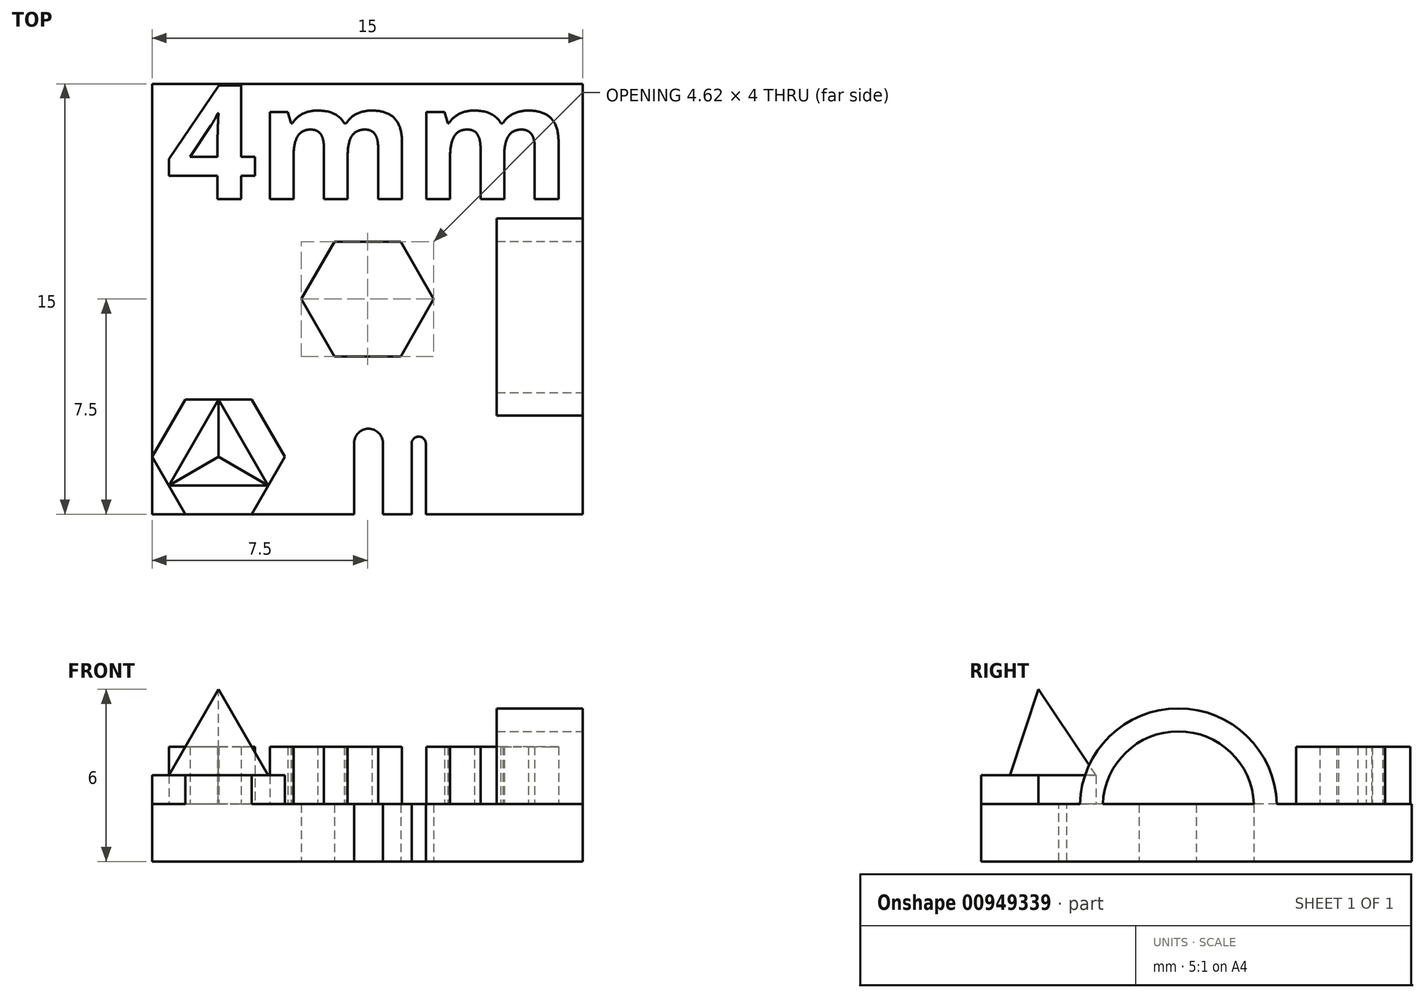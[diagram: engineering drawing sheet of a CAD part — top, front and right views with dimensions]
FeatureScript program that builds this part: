
annotation { "Feature Type Name" : "Feature", "Feature Type Description" : "" }
export const myFeature = defineFeature(function(context is Context, id is Id, definition is map)
    precondition{}
    {
        {
            var Q0;
            Q0=qCreatedBy(makeId("Top.planeOp"),FACE);
            var sketch = newSketch(context, id + "F0", { "sketchPlane" : qUnion([Q0])});
            skLineSegment(sketch, "E0.bottom", {"start": v(-7.5, 7.5) * mm, "end": v(7.5, 7.5) * mm});
            skLineSegment(sketch, "E0.top", {"start": v(-7.5, -7.5) * mm, "end": v(7.5, -7.5) * mm});
            skLineSegment(sketch, "E0.left", {"start": v(-7.5, 7.5) * mm, "end": v(-7.5, -7.5) * mm});
            skLineSegment(sketch, "E0.right", {"start": v(7.5, 7.5) * mm, "end": v(7.5, -7.5) * mm});
            skPoint(sketch, "E0.middle", {"position": v(0, 0) * mm});
            skCircle(sketch, "E1", {"center": v(0, 0) * mm, "radius": 2.3 * mm, "construction": true});
            skLineSegment(sketch, "E2", {"start": v(-1.15, 2) * mm, "end": v(1.15, 2) * mm});
            skLineSegment(sketch, "E3", {"start": v(1.15, 2) * mm, "end": v(2.3, 0) * mm});
            skLineSegment(sketch, "E4", {"start": v(2.3, 0) * mm, "end": v(1.15, -2) * mm});
            skLineSegment(sketch, "E5", {"start": v(1.15, -2) * mm, "end": v(-1.15, -2) * mm});
            skLineSegment(sketch, "E6", {"start": v(-1.15, -2) * mm, "end": v(-2.3, 0) * mm});
            skLineSegment(sketch, "E7", {"start": v(-2.3, 0) * mm, "end": v(-1.15, 2) * mm});
            skSolve(sketch);
        }
        {
            var Q0;
            Q0 = qSketchRegion(id + "F0", true);
            extrude(context, id + "F1", {"entities" : qUnion([Q0]), "depth" : 2 * mm, "offsetDistance" : 25 * mm});
        }
        {
            var Q0;
            Q0=qCreatedBy(makeId("Top.planeOp"),FACE);
            var sketch = newSketch(context, id + "F2", { "sketchPlane" : qUnion([Q0])});
            skText(sketch, "E8", { "text": "4mm", "fontName": "OpenSans-Bold.ttf"});
            const initialGuessF2  = {"E8": [-0.00701, 0.00348, 1, 0, 0.004]};
            skSetInitialGuess(sketch, initialGuessF2);
            skSolve(sketch);
        }
        {
            var Q0;
            Q0 = qSketchRegion(id + "F2", true);
            extrude(context, id + "F3", {"entities" : qUnion([Q0]), "operationType" : NewBodyOperationType.ADD, "depth" : 4 * mm, "offsetDistance" : 25 * mm});
        }
        {
            var Q0;
            Q0=qCreatedBy(makeId("Top.planeOp"),FACE);
            var sketch = newSketch(context, id + "F4", { "sketchPlane" : qUnion([Q0])});
            skCircle(sketch, "E9", {"center": v(-5.2, -5.5) * mm, "radius": 2.3 * mm, "construction": true});
            skLineSegment(sketch, "E10", {"start": v(-6.35, -3.5) * mm, "end": v(-4.04, -3.5) * mm});
            skLineSegment(sketch, "E11", {"start": v(-4.04, -3.5) * mm, "end": v(-2.88, -5.5) * mm});
            skLineSegment(sketch, "E12", {"start": v(-2.88, -5.5) * mm, "end": v(-4.04, -7.5) * mm});
            skLineSegment(sketch, "E13", {"start": v(-4.04, -7.5) * mm, "end": v(-6.35, -7.5) * mm});
            skLineSegment(sketch, "E14", {"start": v(-6.35, -7.5) * mm, "end": v(-7.5, -5.5) * mm});
            skLineSegment(sketch, "E15", {"start": v(-7.5, -5.5) * mm, "end": v(-6.35, -3.5) * mm});
            skSolve(sketch);
        }
        {
            var Q0;
            Q0 = qSketchRegion(id + "F4", true);
            extrude(context, id + "F5", {"entities" : qUnion([Q0]), "operationType" : NewBodyOperationType.ADD, "depth" : 3 * mm, "offsetDistance" : 25 * mm});
        }
        {
            var Q0;
            Q0=makeQuery(id+"F1.opExtrude","SWEPT_FACE",FACE,{"disambiguationData":[OSD([sQuery(id+"F0.wireOp",EDGE,"E0.right")])]});
            var sketch = newSketch(context, id + "F6", { "sketchPlane" : qUnion([Q0])});
            skArc(sketch, "E16", {"start": v(2, 2) * mm, "mid": v(-0.63, 4.53) * mm, "end": v(-3.26, 2) * mm});
            skArc(sketch, "E17.0", {"start": v(2.8, 2) * mm, "mid": v(-0.63, 5.33) * mm, "end": v(-4.06, 2) * mm});
            skLineSegment(sketch, "E18", {"start": v(-4.06, 2) * mm, "end": v(-3.26, 2) * mm});
            skLineSegment(sketch, "E19", {"start": v(2, 2) * mm, "end": v(2.8, 2) * mm});
            skSolve(sketch);
        }
        {
            var Q0;
            Q0 = qSketchRegion(id + "F6", true);
            extrude(context, id + "F7", {"entities" : qUnion([Q0]), "operationType" : NewBodyOperationType.ADD, "depth" : -3 * mm, "offsetDistance" : 25 * mm});
        }
        {
            var Q0;
            Q0=makeQuery(id+"F5.opExtrude","CAP_FACE",FACE,{"disambiguationData":[OSD([sQuery(id+"F4.wireOp",EDGE,"E10"),sQuery(id+"F4.wireOp",EDGE,"E11"),sQuery(id+"F4.wireOp",EDGE,"E12"),sQuery(id+"F4.wireOp",EDGE,"E13"),sQuery(id+"F4.wireOp",EDGE,"E14"),sQuery(id+"F4.wireOp",EDGE,"E15")])],"isStart":false});
            cPlane(context, id + "F8", {"entities" : qUnion([Q0]), "cplaneType" : CPlaneType.OFFSET, "offset" : 3 * mm, "width" : 150 * mm, "height" : 150 * mm});
        }
        {
            var Q0;
            Q0=makeQuery(id+"F5.opExtrude","CAP_FACE",FACE,{"disambiguationData":[OSD([sQuery(id+"F4.wireOp",EDGE,"E10"),sQuery(id+"F4.wireOp",EDGE,"E11"),sQuery(id+"F4.wireOp",EDGE,"E12"),sQuery(id+"F4.wireOp",EDGE,"E13"),sQuery(id+"F4.wireOp",EDGE,"E14"),sQuery(id+"F4.wireOp",EDGE,"E15")])],"isStart":false});
            var sketch = newSketch(context, id + "F9", { "sketchPlane" : qUnion([Q0])});
            skCircle(sketch, "E20.cCircle", {"center": v(-5.2, -5.5) * mm, "radius": 1 * mm, "construction": true});
            skLineSegment(sketch, "E20.0", {"start": v(-3.46, -6.5) * mm, "end": v(-6.92, -6.5) * mm});
            skLineSegment(sketch, "E20.1", {"start": v(-6.92, -6.5) * mm, "end": v(-5.2, -3.5) * mm});
            skLineSegment(sketch, "E20.2", {"start": v(-5.2, -3.5) * mm, "end": v(-3.46, -6.5) * mm});
            skPoint(sketch, "E20.0.midPoint", {"position": v(-5.2, -6.5) * mm});
            skSolve(sketch);
        }
        {
            var Q0;
            Q0=qCreatedBy(id+"F8.planeOp",FACE);
            var sketch = newSketch(context, id + "F10", { "sketchPlane" : qUnion([Q0])});
            skPoint(sketch, "E21", {"position": v(-5.19, -5.5) * mm});
            skSolve(sketch);
        }
        {
            var Q0;
            Q0=makeQuery(id+"F9.imprint","IMPRINT",FACE,{"disambiguationData":[TD([[makeQuery(id+"F9.imprint","IMPRINT",EDGE,{"derivedFrom":sQuery(id+"F9.wireOp",EDGE,"E20.0")}),-1.0]])]});
            var Q1;
            Q1=sQuery(id+"F10.wireOp",VERTEX,"E21");
            loft(context, id + "F11", {"sheetProfilesArray" : [{ "sheetProfileEntities" : qUnion([Q0]) }, { "sheetProfileEntities" : qUnion([Q1]) }]});
        }
        {
            var Q0;
            {var subQ0=makeQuery(id+"F3.opExtrude","SWEPT_FACE",FACE,{"disambiguationData":[OSD([sQuery(id+"F2.wireOp",EDGE,"E8.sketch_text.stroke-88")])]});var subQ1=makeQuery(id+"F3.opExtrude","SWEPT_FACE",FACE,{"disambiguationData":[OSD([sQuery(id+"F2.wireOp",EDGE,"E8.sketch_text.stroke-86")])]});var subQ2=makeQuery(id+"F3.opExtrude","SWEPT_FACE",FACE,{"disambiguationData":[OSD([sQuery(id+"F2.wireOp",EDGE,"E8.sketch_text.stroke-85")])]});var subQ3=makeQuery(id+"F3.opExtrude","SWEPT_FACE",FACE,{"disambiguationData":[OSD([sQuery(id+"F2.wireOp",EDGE,"E8.sketch_text.stroke-84")])]});var subQ4=makeQuery(id+"F3.opExtrude","SWEPT_FACE",FACE,{"disambiguationData":[OSD([sQuery(id+"F2.wireOp",EDGE,"E8.sketch_text.stroke-83")])]});var subQ5=makeQuery(id+"F3.opExtrude","SWEPT_FACE",FACE,{"disambiguationData":[OSD([sQuery(id+"F2.wireOp",EDGE,"E8.sketch_text.stroke-82")])]});var subQ6=makeQuery(id+"F3.opExtrude","SWEPT_FACE",FACE,{"disambiguationData":[OSD([sQuery(id+"F2.wireOp",EDGE,"E8.sketch_text.stroke-81")])]});var subQ7=makeQuery(id+"F3.opExtrude","SWEPT_FACE",FACE,{"disambiguationData":[OSD([sQuery(id+"F2.wireOp",EDGE,"E8.sketch_text.stroke-70")])]});var subQ8=makeQuery(id+"F3.opExtrude","SWEPT_FACE",FACE,{"disambiguationData":[OSD([sQuery(id+"F2.wireOp",EDGE,"E8.sketch_text.stroke-68")])]});var subQ9=makeQuery(id+"F3.opExtrude","SWEPT_FACE",FACE,{"disambiguationData":[OSD([sQuery(id+"F2.wireOp",EDGE,"E8.sketch_text.stroke-67")])]});var subQ10=makeQuery(id+"F3.opExtrude","SWEPT_FACE",FACE,{"disambiguationData":[OSD([sQuery(id+"F2.wireOp",EDGE,"E8.sketch_text.stroke-66")])]});var subQ11=makeQuery(id+"F3.opExtrude","SWEPT_FACE",FACE,{"disambiguationData":[OSD([sQuery(id+"F2.wireOp",EDGE,"E8.sketch_text.stroke-65")])]});var subQ12=makeQuery(id+"F3.opExtrude","SWEPT_FACE",FACE,{"disambiguationData":[OSD([sQuery(id+"F2.wireOp",EDGE,"E8.sketch_text.stroke-64")])]});var subQ13=makeQuery(id+"F3.opExtrude","SWEPT_FACE",FACE,{"disambiguationData":[OSD([sQuery(id+"F2.wireOp",EDGE,"E8.sketch_text.stroke-63")])]});var subQ14=makeQuery(id+"F3.opExtrude","SWEPT_FACE",FACE,{"disambiguationData":[OSD([sQuery(id+"F2.wireOp",EDGE,"E8.sketch_text.stroke-62")])]});var subQ15=makeQuery(id+"F3.opExtrude","SWEPT_FACE",FACE,{"disambiguationData":[OSD([sQuery(id+"F2.wireOp",EDGE,"E8.sketch_text.stroke-61")])]});var subQ16=makeQuery(id+"F3.opExtrude","SWEPT_FACE",FACE,{"disambiguationData":[OSD([sQuery(id+"F2.wireOp",EDGE,"E8.sketch_text.stroke-60")])]});var subQ17=makeQuery(id+"F3.opExtrude","SWEPT_FACE",FACE,{"disambiguationData":[OSD([sQuery(id+"F2.wireOp",EDGE,"E8.sketch_text.stroke-53")])]});var subQ18=makeQuery(id+"F3.opExtrude","SWEPT_FACE",FACE,{"disambiguationData":[OSD([sQuery(id+"F2.wireOp",EDGE,"E8.sketch_text.stroke-52")])]});var subQ19=makeQuery(id+"F3.opExtrude","SWEPT_FACE",FACE,{"disambiguationData":[OSD([sQuery(id+"F2.wireOp",EDGE,"E8.sketch_text.stroke-51")])]});var subQ20=makeQuery(id+"F3.opExtrude","SWEPT_FACE",FACE,{"disambiguationData":[OSD([sQuery(id+"F2.wireOp",EDGE,"E8.sketch_text.stroke-50")])]});var subQ21=makeQuery(id+"F3.opExtrude","SWEPT_FACE",FACE,{"disambiguationData":[OSD([sQuery(id+"F2.wireOp",EDGE,"E8.sketch_text.stroke-49")])]});var subQ22=makeQuery(id+"F3.opExtrude","SWEPT_FACE",FACE,{"disambiguationData":[OSD([sQuery(id+"F2.wireOp",EDGE,"E8.sketch_text.stroke-48")])]});var subQ23=makeQuery(id+"F3.opExtrude","SWEPT_FACE",FACE,{"disambiguationData":[OSD([sQuery(id+"F2.wireOp",EDGE,"E8.sketch_text.stroke-47")])]});var subQ24=makeQuery(id+"F3.opExtrude","SWEPT_FACE",FACE,{"disambiguationData":[OSD([sQuery(id+"F2.wireOp",EDGE,"E8.sketch_text.stroke-46")])]});var subQ25=makeQuery(id+"F3.opExtrude","SWEPT_FACE",FACE,{"disambiguationData":[OSD([sQuery(id+"F2.wireOp",EDGE,"E8.sketch_text.stroke-45")])]});var subQ26=makeQuery(id+"F3.opExtrude","SWEPT_FACE",FACE,{"disambiguationData":[OSD([sQuery(id+"F2.wireOp",EDGE,"E8.sketch_text.stroke-44")])]});var subQ27=makeQuery(id+"F3.opExtrude","SWEPT_FACE",FACE,{"disambiguationData":[OSD([sQuery(id+"F2.wireOp",EDGE,"E8.sketch_text.stroke-43")])]});var subQ28=makeQuery(id+"F3.opExtrude","SWEPT_FACE",FACE,{"disambiguationData":[OSD([sQuery(id+"F2.wireOp",EDGE,"E8.sketch_text.stroke-42")])]});var subQ29=makeQuery(id+"F3.opExtrude","SWEPT_FACE",FACE,{"disambiguationData":[OSD([sQuery(id+"F2.wireOp",EDGE,"E8.sketch_text.stroke-41")])]});var subQ30=makeQuery(id+"F3.opExtrude","SWEPT_FACE",FACE,{"disambiguationData":[OSD([sQuery(id+"F2.wireOp",EDGE,"E8.sketch_text.stroke-40")])]});var subQ31=makeQuery(id+"F3.opExtrude","SWEPT_FACE",FACE,{"disambiguationData":[OSD([sQuery(id+"F2.wireOp",EDGE,"E8.sketch_text.stroke-10")])]});var subQ32=makeQuery(id+"F3.opExtrude","SWEPT_FACE",FACE,{"disambiguationData":[OSD([sQuery(id+"F2.wireOp",EDGE,"E8.sketch_text.stroke-9")])]});var subQ33=makeQuery(id+"F3.opExtrude","SWEPT_FACE",FACE,{"disambiguationData":[OSD([sQuery(id+"F2.wireOp",EDGE,"E8.sketch_text.stroke-95")])]});var subQ34=makeQuery(id+"F3.opExtrude","SWEPT_FACE",FACE,{"disambiguationData":[OSD([sQuery(id+"F2.wireOp",EDGE,"E8.sketch_text.stroke-8")])]});var subQ35=makeQuery(id+"F3.opExtrude","SWEPT_FACE",FACE,{"disambiguationData":[OSD([sQuery(id+"F2.wireOp",EDGE,"E8.sketch_text.stroke-94")])]});var subQ36=makeQuery(id+"F3.opExtrude","SWEPT_FACE",FACE,{"disambiguationData":[OSD([sQuery(id+"F2.wireOp",EDGE,"E8.sketch_text.stroke-7")])]});var subQ37=makeQuery(id+"F3.opExtrude","SWEPT_FACE",FACE,{"disambiguationData":[OSD([sQuery(id+"F2.wireOp",EDGE,"E8.sketch_text.stroke-93")])]});var subQ38=makeQuery(id+"F3.opExtrude","SWEPT_FACE",FACE,{"disambiguationData":[OSD([sQuery(id+"F2.wireOp",EDGE,"E8.sketch_text.stroke-6")])]});var subQ39=makeQuery(id+"F3.opExtrude","SWEPT_FACE",FACE,{"disambiguationData":[OSD([sQuery(id+"F2.wireOp",EDGE,"E8.sketch_text.stroke-92")])]});var subQ40=makeQuery(id+"F3.opExtrude","SWEPT_FACE",FACE,{"disambiguationData":[OSD([sQuery(id+"F2.wireOp",EDGE,"E8.sketch_text.stroke-5")])]});var subQ41=makeQuery(id+"F3.opExtrude","SWEPT_FACE",FACE,{"disambiguationData":[OSD([sQuery(id+"F2.wireOp",EDGE,"E8.sketch_text.stroke-80")])]});var subQ42=sQuery(id+"F0.wireOp",EDGE,"E7");var subQ43=makeQuery(id+"F1.opExtrude","SWEPT_FACE",FACE,{"disambiguationData":[OSD([subQ42])]});var subQ44=makeQuery(id+"F3.opExtrude","SWEPT_FACE",FACE,{"disambiguationData":[OSD([sQuery(id+"F2.wireOp",EDGE,"E8.sketch_text.stroke-87")])]});var subQ45=makeQuery(id+"F3.opExtrude","SWEPT_FACE",FACE,{"disambiguationData":[OSD([sQuery(id+"F2.wireOp",EDGE,"E8.sketch_text.stroke-0")])]});var subQ46=makeQuery(id+"F3.opExtrude","SWEPT_FACE",FACE,{"disambiguationData":[OSD([sQuery(id+"F2.wireOp",EDGE,"E8.sketch_text.stroke-73")])]});var subQ47=sQuery(id+"F0.wireOp",EDGE,"E0.left");var subQ48=makeQuery(id+"F1.opExtrude","SWEPT_FACE",FACE,{"disambiguationData":[OSD([subQ47])]});var subQ49=makeQuery(id+"F3.opExtrude","SWEPT_FACE",FACE,{"disambiguationData":[OSD([sQuery(id+"F2.wireOp",EDGE,"E8.sketch_text.stroke-19")])]});var subQ50=makeQuery(id+"F3.opExtrude","SWEPT_FACE",FACE,{"disambiguationData":[OSD([sQuery(id+"F2.wireOp",EDGE,"E8.sketch_text.stroke-72")])]});var subQ51=sQuery(id+"F0.wireOp",EDGE,"E0.top");var subQ52=makeQuery(id+"F1.opExtrude","SWEPT_FACE",FACE,{"disambiguationData":[OSD([subQ51])]});var subQ53=makeQuery(id+"F3.opExtrude","SWEPT_FACE",FACE,{"disambiguationData":[OSD([sQuery(id+"F2.wireOp",EDGE,"E8.sketch_text.stroke-18")])]});var subQ54=makeQuery(id+"F3.opExtrude","SWEPT_FACE",FACE,{"disambiguationData":[OSD([sQuery(id+"F2.wireOp",EDGE,"E8.sketch_text.stroke-71")])]});var subQ55=sQuery(id+"F0.wireOp",EDGE,"E6");var subQ56=sQuery(id+"F0.wireOp",EDGE,"E5");var subQ57=sQuery(id+"F0.wireOp",EDGE,"E4");var subQ58=sQuery(id+"F0.wireOp",EDGE,"E3");var subQ59=sQuery(id+"F0.wireOp",EDGE,"E2");var subQ60=sQuery(id+"F0.wireOp",EDGE,"E0.right");var subQ61=sQuery(id+"F0.wireOp",EDGE,"E0.bottom");var subQ62=makeQuery(id+"F1.opExtrude","CAP_FACE",FACE,{"disambiguationData":[OSD([subQ61,subQ51,subQ47,subQ60,subQ59,subQ58,subQ57,subQ56,subQ55,subQ42])],"isStart":false});var subQ63=makeQuery(id+"F3.opExtrude","SWEPT_FACE",FACE,{"disambiguationData":[OSD([sQuery(id+"F2.wireOp",EDGE,"E8.sketch_text.stroke-17")])]});var subQ64=makeQuery(id+"F3.opExtrude","SWEPT_FACE",FACE,{"disambiguationData":[OSD([sQuery(id+"F2.wireOp",EDGE,"E8.sketch_text.stroke-69")])]});var subQ65=makeQuery(id+"F1.opExtrude","SWEPT_FACE",FACE,{"disambiguationData":[OSD([subQ61])]});var subQ66=makeQuery(id+"F3.opExtrude","SWEPT_FACE",FACE,{"disambiguationData":[OSD([sQuery(id+"F2.wireOp",EDGE,"E8.sketch_text.stroke-15")])]});var subQ67=makeQuery(id+"F3.opExtrude","SWEPT_FACE",FACE,{"disambiguationData":[OSD([sQuery(id+"F2.wireOp",EDGE,"E8.sketch_text.stroke-74")])]});var subQ68=makeQuery(id+"F1.opExtrude","SWEPT_FACE",FACE,{"disambiguationData":[OSD([subQ60])]});var subQ69=makeQuery(id+"F3.opExtrude","SWEPT_FACE",FACE,{"disambiguationData":[OSD([sQuery(id+"F2.wireOp",EDGE,"E8.sketch_text.stroke-20")])]});var subQ70=makeQuery(id+"F3.opExtrude","SWEPT_FACE",FACE,{"disambiguationData":[OSD([sQuery(id+"F2.wireOp",EDGE,"E8.sketch_text.stroke-75")])]});var subQ71=makeQuery(id+"F1.opExtrude","SWEPT_FACE",FACE,{"disambiguationData":[OSD([subQ59])]});var subQ72=makeQuery(id+"F3.opExtrude","SWEPT_FACE",FACE,{"disambiguationData":[OSD([sQuery(id+"F2.wireOp",EDGE,"E8.sketch_text.stroke-21")])]});var subQ73=makeQuery(id+"F3.opExtrude","SWEPT_FACE",FACE,{"disambiguationData":[OSD([sQuery(id+"F2.wireOp",EDGE,"E8.sketch_text.stroke-1")])]});var subQ74=makeQuery(id+"F3.opExtrude","SWEPT_FACE",FACE,{"disambiguationData":[OSD([sQuery(id+"F2.wireOp",EDGE,"E8.sketch_text.stroke-76")])]});var subQ75=makeQuery(id+"F1.opExtrude","SWEPT_FACE",FACE,{"disambiguationData":[OSD([subQ58])]});var subQ76=makeQuery(id+"F3.opExtrude","SWEPT_FACE",FACE,{"disambiguationData":[OSD([sQuery(id+"F2.wireOp",EDGE,"E8.sketch_text.stroke-22")])]});var subQ77=makeQuery(id+"F3.opExtrude","SWEPT_FACE",FACE,{"disambiguationData":[OSD([sQuery(id+"F2.wireOp",EDGE,"E8.sketch_text.stroke-89")])]});var subQ78=makeQuery(id+"F3.opExtrude","SWEPT_FACE",FACE,{"disambiguationData":[OSD([sQuery(id+"F2.wireOp",EDGE,"E8.sketch_text.stroke-2")])]});var subQ79=makeQuery(id+"F3.opExtrude","SWEPT_FACE",FACE,{"disambiguationData":[OSD([sQuery(id+"F2.wireOp",EDGE,"E8.sketch_text.stroke-77")])]});var subQ80=makeQuery(id+"F1.opExtrude","SWEPT_FACE",FACE,{"disambiguationData":[OSD([subQ57])]});var subQ81=makeQuery(id+"F3.opExtrude","SWEPT_FACE",FACE,{"disambiguationData":[OSD([sQuery(id+"F2.wireOp",EDGE,"E8.sketch_text.stroke-23")])]});var subQ82=makeQuery(id+"F3.opExtrude","SWEPT_FACE",FACE,{"disambiguationData":[OSD([sQuery(id+"F2.wireOp",EDGE,"E8.sketch_text.stroke-90")])]});var subQ83=makeQuery(id+"F3.opExtrude","SWEPT_FACE",FACE,{"disambiguationData":[OSD([sQuery(id+"F2.wireOp",EDGE,"E8.sketch_text.stroke-3")])]});var subQ84=makeQuery(id+"F3.opExtrude","SWEPT_FACE",FACE,{"disambiguationData":[OSD([sQuery(id+"F2.wireOp",EDGE,"E8.sketch_text.stroke-78")])]});var subQ85=makeQuery(id+"F1.opExtrude","SWEPT_FACE",FACE,{"disambiguationData":[OSD([subQ56])]});var subQ86=makeQuery(id+"F3.opExtrude","SWEPT_FACE",FACE,{"disambiguationData":[OSD([sQuery(id+"F2.wireOp",EDGE,"E8.sketch_text.stroke-24")])]});var subQ87=makeQuery(id+"F3.opExtrude","SWEPT_FACE",FACE,{"disambiguationData":[OSD([sQuery(id+"F2.wireOp",EDGE,"E8.sketch_text.stroke-91")])]});var subQ88=makeQuery(id+"F3.opExtrude","SWEPT_FACE",FACE,{"disambiguationData":[OSD([sQuery(id+"F2.wireOp",EDGE,"E8.sketch_text.stroke-4")])]});var subQ89=makeQuery(id+"F3.opExtrude","SWEPT_FACE",FACE,{"disambiguationData":[OSD([sQuery(id+"F2.wireOp",EDGE,"E8.sketch_text.stroke-79")])]});var subQ90=makeQuery(id+"F1.opExtrude","SWEPT_FACE",FACE,{"disambiguationData":[OSD([subQ55])]});var subQ91=makeQuery(id+"F3.opExtrude","SWEPT_FACE",FACE,{"disambiguationData":[OSD([sQuery(id+"F2.wireOp",EDGE,"E8.sketch_text.stroke-25")])]});var subQ92=makeQuery(id+"F3.opExtrude","SWEPT_FACE",FACE,{"disambiguationData":[OSD([sQuery(id+"F2.wireOp",EDGE,"E8.sketch_text.stroke-11")])]});var subQ93=makeQuery(id+"F3.opExtrude","SWEPT_FACE",FACE,{"disambiguationData":[OSD([sQuery(id+"F2.wireOp",EDGE,"E8.sketch_text.stroke-12")])]});var subQ94=makeQuery(id+"F3.opExtrude","SWEPT_FACE",FACE,{"disambiguationData":[OSD([sQuery(id+"F2.wireOp",EDGE,"E8.sketch_text.stroke-13")])]});var subQ95=makeQuery(id+"F3.opExtrude","SWEPT_FACE",FACE,{"disambiguationData":[OSD([sQuery(id+"F2.wireOp",EDGE,"E8.sketch_text.stroke-14")])]});var subQ96=makeQuery(id+"F3.opExtrude","SWEPT_FACE",FACE,{"disambiguationData":[OSD([sQuery(id+"F2.wireOp",EDGE,"E8.sketch_text.stroke-16")])]});var subQ97=makeQuery(id+"F3.opExtrude","SWEPT_FACE",FACE,{"disambiguationData":[OSD([sQuery(id+"F2.wireOp",EDGE,"E8.sketch_text.stroke-31")])]});var subQ98=makeQuery(id+"F3.opExtrude","SWEPT_FACE",FACE,{"disambiguationData":[OSD([sQuery(id+"F2.wireOp",EDGE,"E8.sketch_text.stroke-32")])]});var subQ99=makeQuery(id+"F3.opExtrude","SWEPT_FACE",FACE,{"disambiguationData":[OSD([sQuery(id+"F2.wireOp",EDGE,"E8.sketch_text.stroke-33")])]});var subQ100=makeQuery(id+"F3.opExtrude","SWEPT_FACE",FACE,{"disambiguationData":[OSD([sQuery(id+"F2.wireOp",EDGE,"E8.sketch_text.stroke-34")])]});var subQ101=makeQuery(id+"F3.opExtrude","SWEPT_FACE",FACE,{"disambiguationData":[OSD([sQuery(id+"F2.wireOp",EDGE,"E8.sketch_text.stroke-35")])]});var subQ102=makeQuery(id+"F3.opExtrude","SWEPT_FACE",FACE,{"disambiguationData":[OSD([sQuery(id+"F2.wireOp",EDGE,"E8.sketch_text.stroke-36")])]});var subQ103=makeQuery(id+"F3.opExtrude","SWEPT_FACE",FACE,{"disambiguationData":[OSD([sQuery(id+"F2.wireOp",EDGE,"E8.sketch_text.stroke-37")])]});var subQ104=makeQuery(id+"F3.opExtrude","SWEPT_FACE",FACE,{"disambiguationData":[OSD([sQuery(id+"F2.wireOp",EDGE,"E8.sketch_text.stroke-38")])]});var subQ105=makeQuery(id+"F3.opExtrude","SWEPT_FACE",FACE,{"disambiguationData":[OSD([sQuery(id+"F2.wireOp",EDGE,"E8.sketch_text.stroke-39")])]});var subQ106=makeQuery(id+"F3.opExtrude","SWEPT_FACE",FACE,{"disambiguationData":[OSD([sQuery(id+"F2.wireOp",EDGE,"E8.sketch_text.stroke-96")])]});var subQ107=makeQuery(id+"F3.opExtrude","SWEPT_FACE",FACE,{"disambiguationData":[OSD([sQuery(id+"F2.wireOp",EDGE,"E8.sketch_text.stroke-97")])]});var subQ108=makeQuery(id+"F3.opExtrude","SWEPT_FACE",FACE,{"disambiguationData":[OSD([sQuery(id+"F2.wireOp",EDGE,"E8.sketch_text.stroke-98")])]});var subQ109=makeQuery(id+"F3.opExtrude","SWEPT_FACE",FACE,{"disambiguationData":[OSD([sQuery(id+"F2.wireOp",EDGE,"E8.sketch_text.stroke-99")])]});var subQ110=makeQuery(id+"F3.opExtrude","SWEPT_FACE",FACE,{"disambiguationData":[OSD([sQuery(id+"F2.wireOp",EDGE,"E8.sketch_text.stroke-100")])]});var subQ111=makeQuery(id+"F3.opExtrude","SWEPT_FACE",FACE,{"disambiguationData":[OSD([sQuery(id+"F2.wireOp",EDGE,"E8.sketch_text.stroke-101")])]});var subQ112=makeQuery(id+"F3.opExtrude","SWEPT_FACE",FACE,{"disambiguationData":[OSD([sQuery(id+"F2.wireOp",EDGE,"E8.sketch_text.stroke-102")])]});var subQ113=makeQuery(id+"F3.opExtrude","SWEPT_FACE",FACE,{"disambiguationData":[OSD([sQuery(id+"F2.wireOp",EDGE,"E8.sketch_text.stroke-103")])]});var subQ114=makeQuery(id+"F3.opExtrude","SWEPT_FACE",FACE,{"disambiguationData":[OSD([sQuery(id+"F2.wireOp",EDGE,"E8.sketch_text.stroke-104")])]});var subQ115=makeQuery(id+"F3.opExtrude","SWEPT_FACE",FACE,{"disambiguationData":[OSD([sQuery(id+"F2.wireOp",EDGE,"E8.sketch_text.stroke-105")])]});var subQ116=makeQuery(id+"F3.opExtrude","SWEPT_FACE",FACE,{"disambiguationData":[OSD([sQuery(id+"F2.wireOp",EDGE,"E8.sketch_text.stroke-106")])]});var subQ117=makeQuery(id+"F3.opExtrude","SWEPT_FACE",FACE,{"disambiguationData":[OSD([sQuery(id+"F2.wireOp",EDGE,"E8.sketch_text.stroke-107")])]});var subQ118=makeQuery(id+"F3.opExtrude","SWEPT_FACE",FACE,{"disambiguationData":[OSD([sQuery(id+"F2.wireOp",EDGE,"E8.sketch_text.stroke-108")])]});var subQ119=makeQuery(id+"F3.opExtrude","SWEPT_FACE",FACE,{"disambiguationData":[OSD([sQuery(id+"F2.wireOp",EDGE,"E8.sketch_text.stroke-109")])]});var subQ120=makeQuery(id+"F3.opExtrude","SWEPT_FACE",FACE,{"disambiguationData":[OSD([sQuery(id+"F2.wireOp",EDGE,"E8.sketch_text.stroke-110")])]});var subQ121=makeQuery(id+"F3.opExtrude","SWEPT_FACE",FACE,{"disambiguationData":[OSD([sQuery(id+"F2.wireOp",EDGE,"E8.sketch_text.stroke-111")])]});var subQ122=makeQuery(id+"F3.opExtrude","SWEPT_FACE",FACE,{"disambiguationData":[OSD([sQuery(id+"F2.wireOp",EDGE,"E8.sketch_text.stroke-112")])]});var subQ123=makeQuery(id+"F3.opExtrude","SWEPT_FACE",FACE,{"disambiguationData":[OSD([sQuery(id+"F2.wireOp",EDGE,"E8.sketch_text.stroke-113")])]});var subQ124=makeQuery(id+"F3.opExtrude","SWEPT_FACE",FACE,{"disambiguationData":[OSD([sQuery(id+"F2.wireOp",EDGE,"E8.sketch_text.stroke-114")])]});var subQ125=makeQuery(id+"F3.opExtrude","SWEPT_FACE",FACE,{"disambiguationData":[OSD([sQuery(id+"F2.wireOp",EDGE,"E8.sketch_text.stroke-115")])]});Q0=makeQuery(id+"F5.boolean.opBoolean","SPLIT",FACE,{"disambiguationData":[TD([subQ65,subQ62,subQ52,subQ48,subQ68,subQ71,subQ75,subQ80,subQ85,subQ90,subQ43,subQ45,subQ73,subQ78,subQ83,subQ88,subQ40,subQ38,subQ36,subQ34,subQ32,subQ31,subQ92,subQ93,subQ94,subQ95,subQ66,subQ96,subQ63,subQ53,subQ49,subQ69,subQ72,subQ76,subQ81,subQ86,subQ91,subQ97,subQ98,subQ99,subQ100,subQ101,subQ102,subQ103,subQ104,subQ105,subQ30,subQ29,subQ28,subQ27,subQ26,subQ25,subQ24,subQ23,subQ22,subQ21,subQ20,subQ19,subQ18,subQ17,subQ16,subQ15,subQ14,subQ13,subQ12,subQ11,subQ10,subQ9,subQ8,subQ64,subQ7,subQ54,subQ50,subQ46,subQ67,subQ70,subQ74,subQ79,subQ84,subQ89,subQ41,subQ6,subQ5,subQ4,subQ3,subQ2,subQ1,subQ44,subQ0,subQ77,subQ82,subQ87,subQ39,subQ37,subQ35,subQ33,subQ106,subQ107,subQ108,subQ109,subQ110,subQ111,subQ112,subQ113,subQ114,subQ115,subQ116,subQ117,subQ118,subQ119,subQ120,subQ121,subQ122,subQ123,subQ124,subQ125,makeQuery(id+"F5.opExtrude","SWEPT_FACE",FACE,{"disambiguationData":[OSD([sQuery(id+"F4.wireOp",EDGE,"E10")])]}),makeQuery(id+"F5.opExtrude","SWEPT_FACE",FACE,{"disambiguationData":[OSD([sQuery(id+"F4.wireOp",EDGE,"E11")])]}),makeQuery(id+"F5.opExtrude","SWEPT_FACE",FACE,{"disambiguationData":[OSD([sQuery(id+"F4.wireOp",EDGE,"E12")])]}),makeQuery(id+"F5.opExtrude","SWEPT_FACE",FACE,{"disambiguationData":[OSD([sQuery(id+"F4.wireOp",EDGE,"E13")])]}),makeQuery(id+"F5.opExtrude","SWEPT_FACE",FACE,{"disambiguationData":[OSD([sQuery(id+"F4.wireOp",EDGE,"E14")])]}),makeQuery(id+"F5.opExtrude","SWEPT_FACE",FACE,{"disambiguationData":[OSD([sQuery(id+"F4.wireOp",EDGE,"E15")])]})])],"derivedFrom":makeQuery(id+"F3.boolean.opBoolean","SPLIT",FACE,{"disambiguationData":[TD([subQ65])],"derivedFrom":subQ62})});}
            var sketch = newSketch(context, id + "F12", { "sketchPlane" : qUnion([Q0])});
            skLineSegment(sketch, "E22", {"start": v(-0.46, -7.5) * mm, "end": v(-0.46, -5.02) * mm});
            skLineSegment(sketch, "E23", {"start": v(0.54, -5.02) * mm, "end": v(0.54, -7.5) * mm});
            skLineSegment(sketch, "E24", {"start": v(1.54, -7.5) * mm, "end": v(1.54, -5.05) * mm});
            skLineSegment(sketch, "E25", {"start": v(2.04, -5.05) * mm, "end": v(2.04, -7.5) * mm});
            skLineSegment(sketch, "E26", {"start": v(-0.46, -7.5) * mm, "end": v(0.54, -7.5) * mm});
            skLineSegment(sketch, "E27", {"start": v(1.54, -7.5) * mm, "end": v(2.04, -7.5) * mm});
            skArc(sketch, "E28", {"start": v(0.54, -5.02) * mm, "mid": v(0.04, -4.52) * mm, "end": v(-0.46, -5.02) * mm});
            skArc(sketch, "E29", {"start": v(2.04, -5.05) * mm, "mid": v(1.79, -4.8) * mm, "end": v(1.54, -5.05) * mm});
            skSolve(sketch);
        }
        {
            var Q0;
            Q0 = qSketchRegion(id + "F12", true);
            extrude(context, id + "F13", {"entities" : qUnion([Q0]), "operationType" : NewBodyOperationType.REMOVE, "oppositeDirection" : true, "depth" : 2 * mm, "offsetDistance" : 25 * mm});
        }
    });
